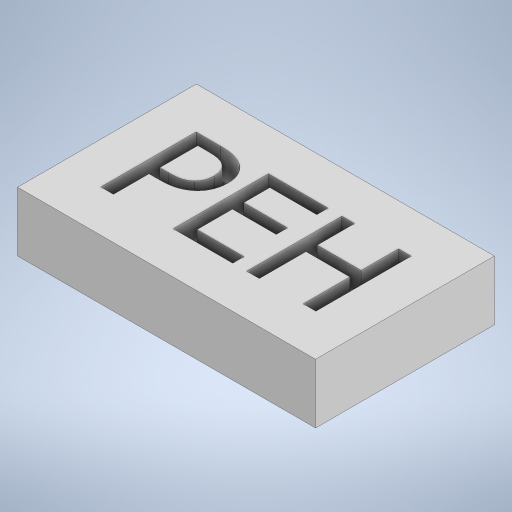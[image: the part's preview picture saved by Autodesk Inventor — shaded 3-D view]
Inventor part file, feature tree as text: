
AUTODESK INVENTOR PART (.ipt)
format: ipt  version: 2024 (Build 280153000, 153)  size: 261,120 bytes
history: native  units: mm
features: other x2, sketch x2, extrude x1
ambient origin geometry x8: Origin, YZ Plane, XZ Plane, XY Plane, X Axis, Y Axis, Z Axis, Center Point
bodies: Body1 (feature_tree)
feature tree (5):
  other  "솔리드1"
  extrude  "돌출1"  Depth=30.0mm
  other  "엠보싱1"
  sketch  "스케치1"
  sketch  "스케치2"
